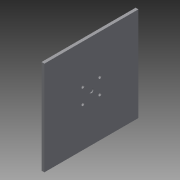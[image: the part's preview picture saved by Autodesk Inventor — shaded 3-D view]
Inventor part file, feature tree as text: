
AUTODESK INVENTOR PART (.ipt)
format: ipt  version: 2014 (Build 180170000, 170)  size: 84,992 bytes
history: native  units: mm
features: extrude x3, sketch x3
ambient origin geometry x8: Origin, YZ Plane, XZ Plane, XY Plane, X Axis, Y Axis, Z Axis, Center Point
bodies: Solid1 (feature_tree)
feature tree (6):
  extrude  "Extrusion1"  Depth=100.0mm
  extrude  "Extrusion2"  Depth=3.0mm TaperAngle=0.0deg
  extrude  "Extrusion3"  [1 undecoded]
  sketch  "Sketch1"  dims[d0=100.0mm d1=100.0mm]
  sketch  "Sketch2"  dims[d2=3.0mm d3=0.0mm d4=3.0mm d5=0.0mm]
  sketch  "Sketch3"  dims[d6=1.0mm d7=0.0mm]
note: 1 required parameter value undecoded (feature->parameter linkage not recoverable at this tier; creation-order binding heuristic only, values carry confidence <= 0.55)
